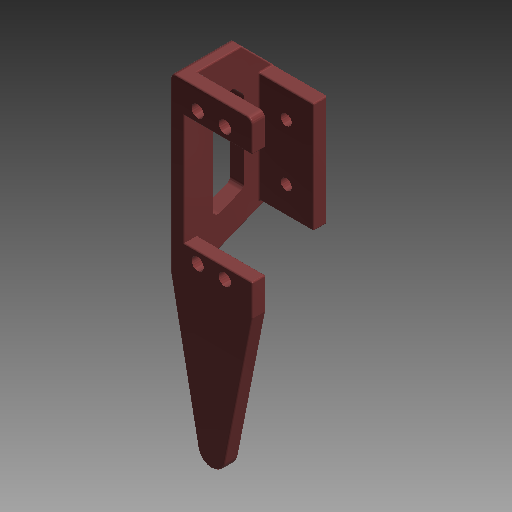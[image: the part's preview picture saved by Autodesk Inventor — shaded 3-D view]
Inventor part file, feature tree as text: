
AUTODESK INVENTOR PART (.ipt)
format: ipt  version: 2017 (Build 210142000, 142)  size: 315,904 bytes
history: native  units: mm (DEFAULTED — no unit token found)
features: sketch x8, extrude x7, fillet x3, draft x1, chamfer x1
ambient origin geometry x8: Origin, YZ Plane, XZ Plane, XY Plane, X Axis, Y Axis, Z Axis, Center Point
bodies: Solid1 (feature_tree)
feature tree (20):
  sketch  "Sketch1"  dims[d0=30.0mm d1=63.5mm]
  extrude  "Extrusion1"  Depth=63.5mm
  extrude  "Extrusion2"  Depth=10.0mm
  extrude  "Extrusion3"  TaperAngle=0.0deg  [1 undecoded]
  extrude  "Extrusion6"  Depth=53.5mm
  extrude  "Extrusion7"  Depth=5.0mm
  extrude  "Extrusion8"  Depth=2.5mm
  draft  "FaceDraft3"
  chamfer  "Chamfer1"  Distance=40.5mm
  fillet  "Fillet4"  Radius=5.0mm
  fillet  "Fillet5"  [1 undecoded]
  extrude  "Extrusion9"  Depth=10.0mm TaperAngle=0.0deg
  fillet  "Fillet6"  Radius=27.5mm
  sketch  "Sketch2"  dims[d2=10.0mm d3=50.0mm]
  sketch  "Sketch3"  dims[d4=5.0mm d5=0.0mm]
  sketch  "Sketch4"  dims[d6=20.0mm d7=53.5mm]
  sketch  "Sketch8"  dims[d8=5.0mm d9=4.5mm]
  sketch  "Sketch9"  dims[d11=2.75mm d12=2.5mm]
  sketch  "Sketch14"  dims[d13=2.75mm]
  sketch  "Sketch15"  dims[d14=2.5mm d15=40.5mm d16=5.0mm d17=0.0mm d18=10.0mm d19=0.0mm d25=27.5mm d26=0.0mm d27=5.0mm d28=20.0mm d29=0.0mm d35=40.5mm d36=4.0mm d37=10.0mm d38=10.0mm d39=0.0mm d40=3.839724mm d41=11.25mm d42=1.25mm d43=45.0deg d44=0.5mm d45=2.0mm d46=10.0mm d47=10.0mm d48=10.0mm d49=10.0mm d50=10.0mm d51=10.0mm d52=10.0mm d53=0.0mm d54=2.0mm]
note: 2 required parameter values undecoded (feature->parameter linkage not recoverable at this tier; creation-order binding heuristic only, values carry confidence <= 0.55)
